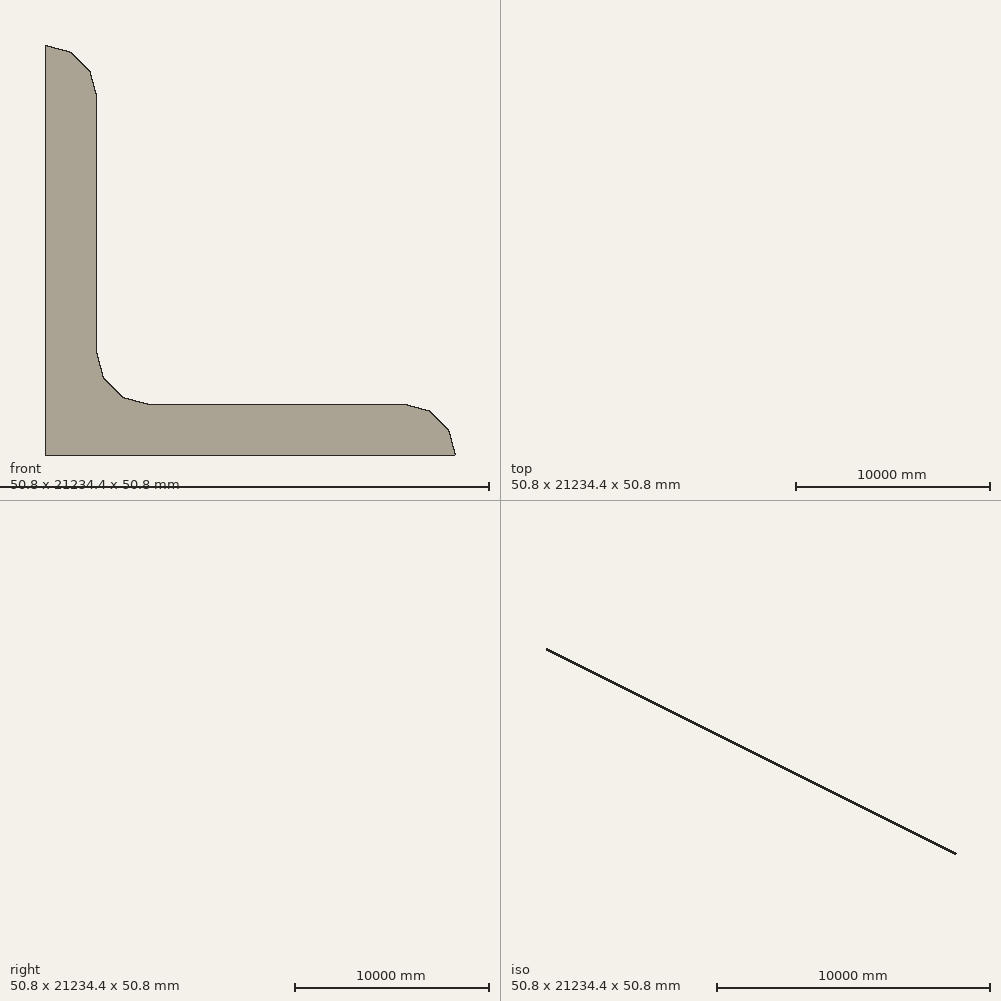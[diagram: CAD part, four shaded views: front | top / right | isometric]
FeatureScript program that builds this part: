
annotation { "Feature Type Name" : "Feature", "Feature Type Description" : "" }
export const myFeature = defineFeature(function(context is Context, id is Id, definition is map)
    precondition{}
    {
        {
            var Q0;
            Q0=qCreatedBy(makeId("Front.planeOp"),FACE);
            var sketch = newSketch(context, id + "F0", { "sketchPlane" : qUnion([Q0])});
            skLineSegment(sketch, "E0.bottom", {"start": v(0, 0) * mm, "end": v(50.8, 0) * mm});
            skLineSegment(sketch, "E1", {"start": v(0, 0) * mm, "end": v(0, 50.8) * mm});
            skLineSegment(sketch, "E2", {"start": v(0, 50.8) * mm, "end": v(0, 50.8) * mm});
            skLineSegment(sketch, "E3", {"start": v(6.35, 44.45) * mm, "end": v(6.35, 12.7) * mm});
            skLineSegment(sketch, "E4", {"start": v(12.7, 6.35) * mm, "end": v(44.45, 6.35) * mm});
            skLineSegment(sketch, "E5", {"start": v(50.8, 0) * mm, "end": v(50.8, 0) * mm});
            skPoint(sketch, "E6.visualSharp", {"position": v(6.35, 50.8) * mm});
            skArc(sketch, "E6.filletArc", {"start": v(6.35, 44.45) * mm, "mid": v(4.5, 48.94) * mm, "end": v(0, 50.8) * mm});
            skPoint(sketch, "E7.visualSharp", {"position": v(50.8, 6.35) * mm});
            skArc(sketch, "E7.filletArc", {"start": v(50.8, 0) * mm, "mid": v(48.94, 4.5) * mm, "end": v(44.45, 6.35) * mm});
            skPoint(sketch, "E8.visualSharp", {"position": v(6.35, 6.35) * mm});
            skArc(sketch, "E8.filletArc", {"start": v(6.35, 12.7) * mm, "mid": v(8.2, 8.2) * mm, "end": v(12.7, 6.35) * mm});
            skSolve(sketch);
        }
        {
            var Q0;
            Q0=qSketchRegion(id+"F0",true);
            extrude(context, id + "F1", {"entities" : qUnion([Q0]), "oppositeDirection" : true, "depth" : 21234.4 * mm});
        }
    });
